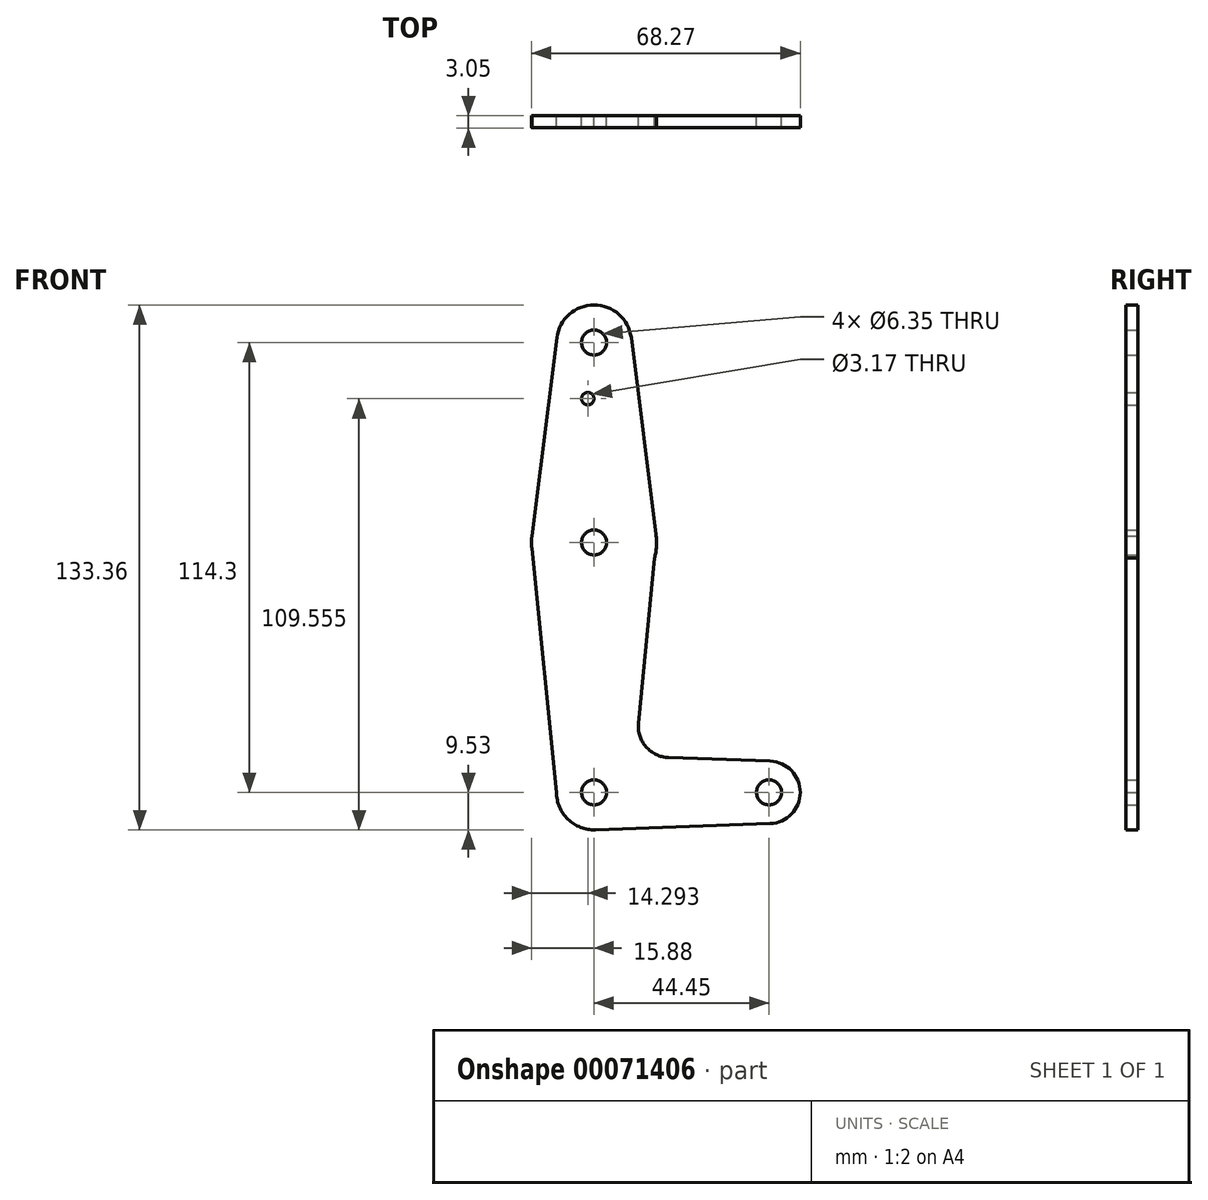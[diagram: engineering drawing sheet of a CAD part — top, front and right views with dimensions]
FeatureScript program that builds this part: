
annotation { "Feature Type Name" : "Feature", "Feature Type Description" : "" }
export const myFeature = defineFeature(function(context is Context, id is Id, definition is map)
    precondition{}
    {
        {
            var Q0;
            Q0=qCreatedBy(makeId("Front.planeOp"),FACE);
            var sketch = newSketch(context, id + "F0", { "sketchPlane" : qUnion([Q0])});
            skLineSegment(sketch, "E0", {"start": v(0, 0) * mm, "end": v(44.45, 0) * mm, "construction": true});
            skLineSegment(sketch, "E1", {"start": v(0, 0) * mm, "end": v(0, 114.3) * mm, "construction": true});
            skCircle(sketch, "E2", {"center": v(0, 114.3) * mm, "radius": 9.53 * mm});
            skCircle(sketch, "E3", {"center": v(0, 63.5) * mm, "radius": 15.88 * mm});
            skCircle(sketch, "E4", {"center": v(0, 0) * mm, "radius": 9.53 * mm});
            skCircle(sketch, "E5", {"center": v(44.45, 0) * mm, "radius": 7.94 * mm});
            skLineSegment(sketch, "E6", {"start": v(-9.45, 115.5) * mm, "end": v(-15.8, 65.13) * mm});
            skLineSegment(sketch, "E7", {"start": v(9.45, 115.5) * mm, "end": v(15.75, 65.48) * mm});
            skLineSegment(sketch, "E8", {"start": v(18.9, 8.86) * mm, "end": v(44.73, 7.93) * mm});
            skLineSegment(sketch, "E9", {"start": v(0.34, -9.52) * mm, "end": v(44.73, -7.93) * mm});
            skCircle(sketch, "E10", {"center": v(-1.59, 100.03) * mm, "radius": 1.59 * mm});
            skPoint(sketch, "E11.newPointB", {"position": v(0.34, 9.52) * mm});
            skCircle(sketch, "E12", {"center": v(0, 114.3) * mm, "radius": 3.18 * mm});
            skCircle(sketch, "E13", {"center": v(0, 63.5) * mm, "radius": 3.18 * mm});
            skCircle(sketch, "E14", {"center": v(0, 0) * mm, "radius": 3.18 * mm});
            skLineSegment(sketch, "E15", {"start": v(15.75, 63.5) * mm, "end": v(11.28, 17.57) * mm});
            skLineSegment(sketch, "E16", {"start": v(-15.8, 65.13) * mm, "end": v(-15.8, 61.91) * mm});
            skLineSegment(sketch, "E17", {"start": v(-15.8, 61.91) * mm, "end": v(-9.57, 0) * mm});
            skLineSegment(sketch, "E18", {"start": v(-9.57, 0) * mm, "end": v(-9.52, 0) * mm});
            skPoint(sketch, "E19.newPointA", {"position": v(9.57, 0) * mm});
            skArc(sketch, "E19.filletArc", {"start": v(11.28, 17.57) * mm, "mid": v(13.21, 11.56) * mm, "end": v(18.9, 8.86) * mm});
            skCircle(sketch, "E20", {"center": v(44.45, 0) * mm, "radius": 3.18 * mm});
            skSolve(sketch);
        }
        {
            var Q0;
            Q0 = qSketchRegion(id + "F0", true);
            extrude(context, id + "F1", {"entities" : qUnion([Q0]), "depth" : 3.05 * mm});
        }
    });
